# Revit family: ledspot3c-e_30w-4000-24d-bl_541001045100
name_source: partatom
category: Leuchten
revit_build: Autodesk Revit 2016 (Build: 20190508_0715(x64)
units: mm (PartAtom-declared; Revit-internal decimal feet)

## family parameters
Basisbauteil = Fläche
Beim Laden mit Abzugskörper schneiden = Nein
Bemaßung runder Anschluss = Durchmesser verwenden
Gemeinsam genutzt = Nein
Lichtquelle = Nein
Raumberechnungspunkt = Nein
Teiletyp = Normal

## types (1)
- LEDSpot3C-E 30W-4000-24D-BL (1 x LED, 2400 lm)
    Approval mark = CE
    Beschreibung = High performance compact track spot with high luminous efficiency and homogeneous light distribution. Simple but sleek design in cylindrical shape with no visible cooling fins. Ideal for retail stores, showrooms, offices and homes thanks to its adjustable light head. Fitting common Global/Nordic Aluminum® 3C Tracks – and many other standard types.
    CIE Flux Codes = 98 100 100 99 100
    Control Gear = Electronic ballast
    Height = 187 mm
    Hersteller = OPPLE
    Lamp Light Flux = 2400 lm
    Lamp count = 1
    Lampe = 1 x LED
    Length = 80 mm  [stored 0.262467 ft]
    Luminous efficacy = 80 lm/W
    ModVariant = Nein
    Modell = 541001045100
    Mounting Place = Ceiling
    Mounting Type = Surface mounted
    Number of Poles = 1
    OnlyDefault = Ja
    Power Factor = 1
    Product Name = LEDSpot3C-E 30W-4000-24D-BL
    Product group = Spot EcoMax 3C
    ProductGroupID = 321
    Protection Class = Protection class II
    Protection Degree = IP 20
    RLX_Detail_Level = 1
    RlxData = <blob elided: 147645 chars, md5=f8799308>
    Scheinlast = 30 VA
    Socket = socket
    Standby Power = 0 W
    System Light Flux = 2398 lm
    System Power = 30 W
    Typenbild = 541001045100.jpg
    Typenkommentare = Product without accessories
    URL = http://relux.com
    VarID = ---
    Voltage = 0 V
    Vorgabe-Ansicht = 1800 mm
    Weight = 0.00 kg
    Width = 113 mm

note: [stored X ft] marks values corroborated as IEEE doubles in the binary element streams (Revit-internal decimal feet)

## geometry (parser evidence)
native form markers: Blend x4, Sweep x13
no freeform markers — native parametric forms only
